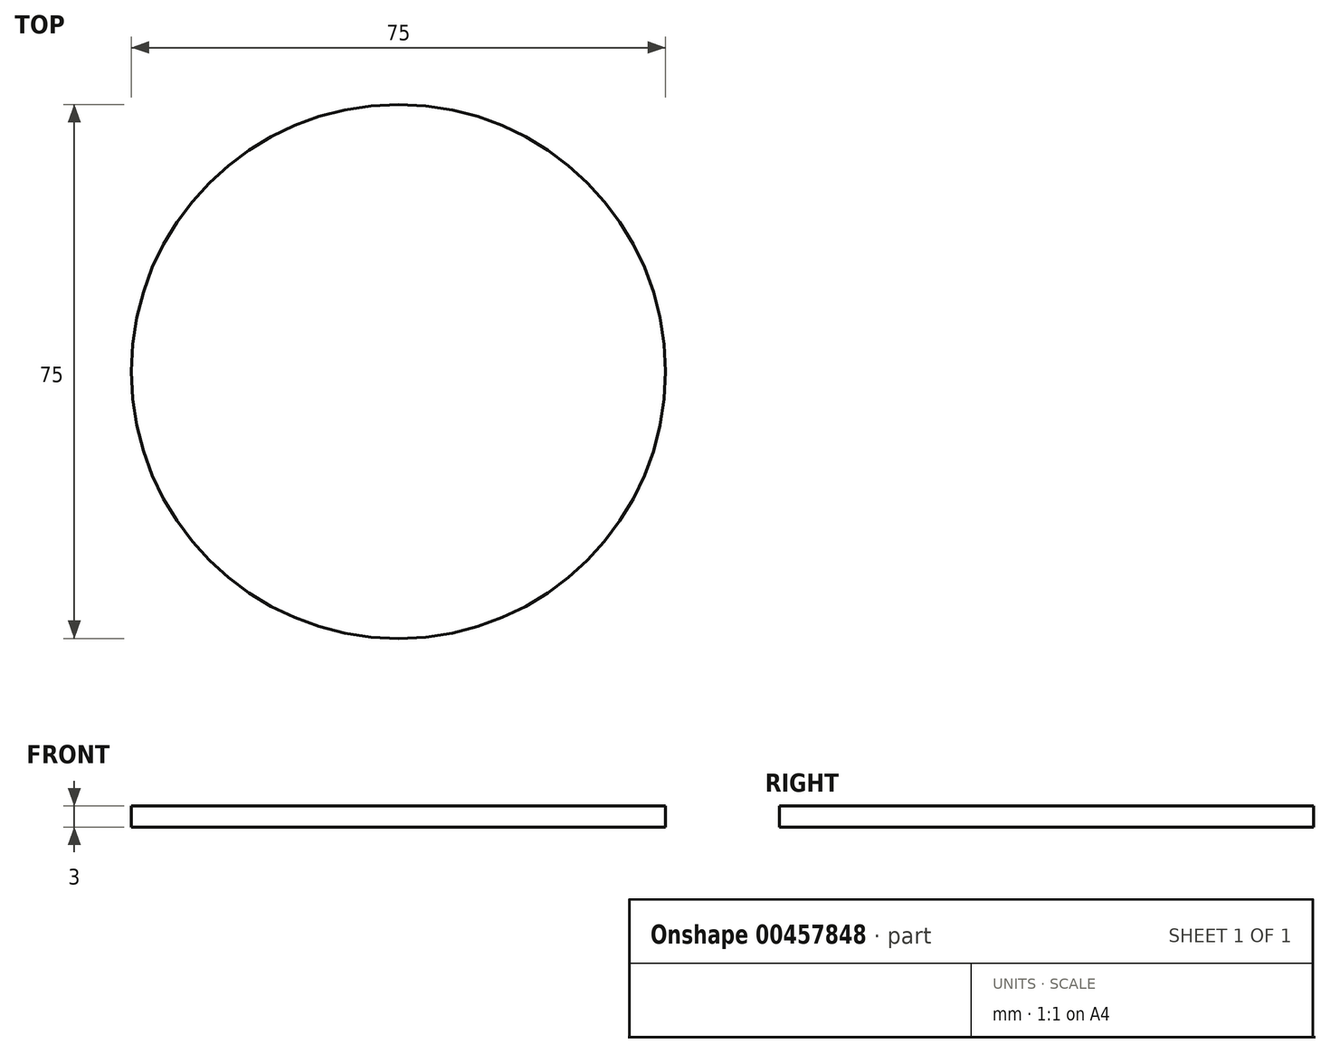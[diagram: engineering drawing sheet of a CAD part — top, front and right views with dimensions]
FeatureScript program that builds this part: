
annotation { "Feature Type Name" : "Feature", "Feature Type Description" : "" }
export const myFeature = defineFeature(function(context is Context, id is Id, definition is map)
    precondition{}
    {
        {
            var Q0;
            Q0=qCreatedBy(makeId("Top.planeOp"),FACE);
            var sketch = newSketch(context, id + "F0", { "sketchPlane" : qUnion([Q0])});
            skCircle(sketch, "E0", {"center": v(0, 0) * mm, "radius": 37.5 * mm});
            skSolve(sketch);
        }
        {
            var Q0;
            Q0=makeQuery(id+"F0.imprint","IMPRINT",FACE,{"disambiguationData":[TD([[makeQuery(id+"F0.imprint","IMPRINT",EDGE,{"derivedFrom":sQuery(id+"F0.wireOp",EDGE,"E0")}),1.0]])]});
            extrude(context, id + "F1", {"entities" : qUnion([Q0]), "depth" : 3 * mm});
        }
    });
